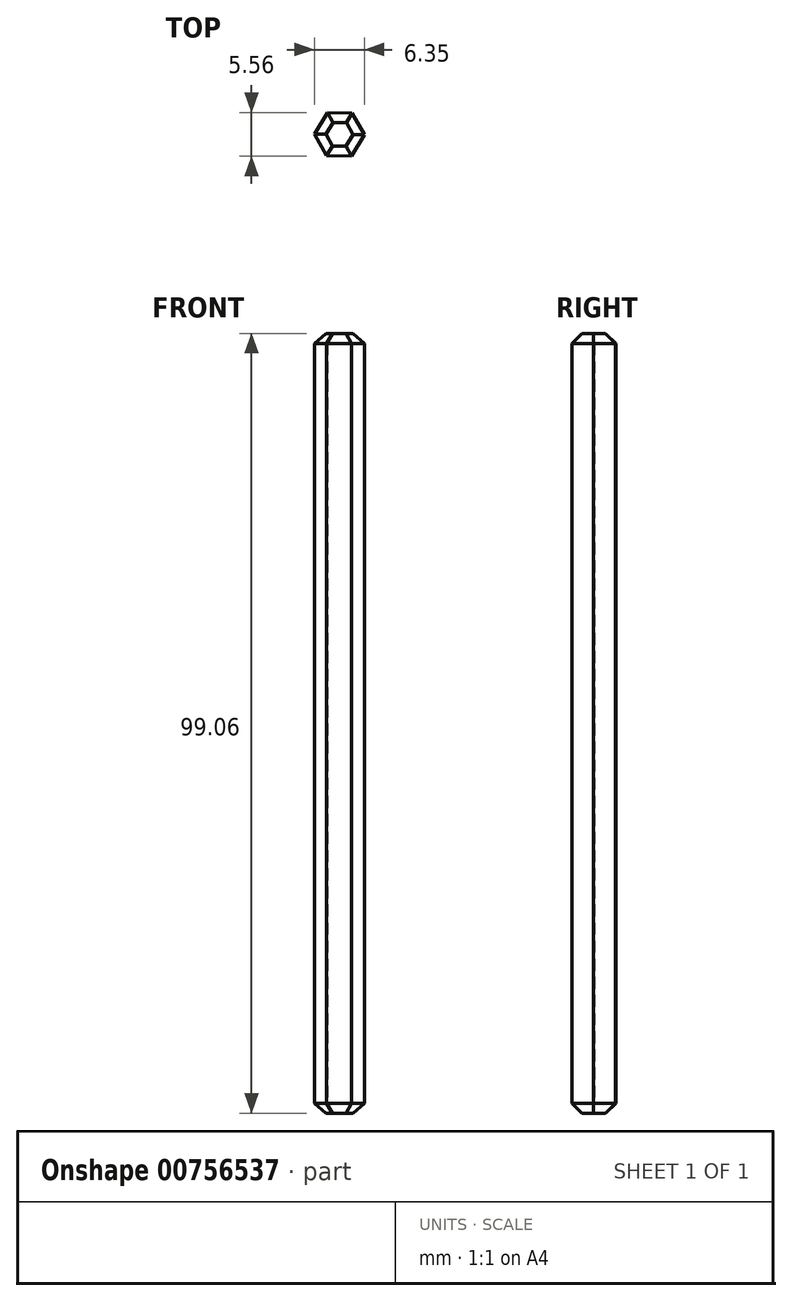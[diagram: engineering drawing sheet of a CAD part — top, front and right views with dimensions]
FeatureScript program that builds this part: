
annotation { "Feature Type Name" : "Feature", "Feature Type Description" : "" }
export const myFeature = defineFeature(function(context is Context, id is Id, definition is map)
    precondition{}
    {
        {
            var Q0;
            Q0=qCreatedBy(makeId("Top.planeOp"),FACE);
            var sketch = newSketch(context, id + "F0", { "sketchPlane" : qUnion([Q0])});
            skCircle(sketch, "E0.cCircle", {"center": v(-0.05, 1.05) * mm, "radius": 3.18 * mm, "construction": true});
            skLineSegment(sketch, "E0.0", {"start": v(-1.69, -1.67) * mm, "end": v(-3.22, 1.1) * mm});
            skLineSegment(sketch, "E0.1", {"start": v(-3.22, 1.1) * mm, "end": v(-1.58, 3.83) * mm});
            skLineSegment(sketch, "E0.2", {"start": v(-1.58, 3.83) * mm, "end": v(1.59, 3.77) * mm});
            skLineSegment(sketch, "E0.3", {"start": v(1.59, 3.77) * mm, "end": v(3.13, 0.99) * mm});
            skLineSegment(sketch, "E0.4", {"start": v(3.13, 0.99) * mm, "end": v(1.49, -1.73) * mm});
            skLineSegment(sketch, "E0.5", {"start": v(1.49, -1.73) * mm, "end": v(-1.69, -1.67) * mm});
            skSolve(sketch);
        }
        {
            var Q0;
            Q0=makeQuery(id+"F0.imprint","IMPRINT",FACE,{"disambiguationData":[TD([[makeQuery(id+"F0.imprint","IMPRINT",EDGE,{"derivedFrom":sQuery(id+"F0.wireOp",EDGE,"E0.0")}),-1.0]])]});
            extrude(context, id + "F1", {"entities" : qUnion([Q0]), "depth" : 99.06 * mm, "offsetDistance" : 25.4 * mm});
        }
        {
            var Q0;
            Q0=makeQuery(id+"F1.opExtrude","CAP_FACE",FACE,{"disambiguationData":[OSD([sQuery(id+"F0.wireOp",EDGE,"E0.0"),sQuery(id+"F0.wireOp",EDGE,"E0.1"),sQuery(id+"F0.wireOp",EDGE,"E0.2"),sQuery(id+"F0.wireOp",EDGE,"E0.3"),sQuery(id+"F0.wireOp",EDGE,"E0.4"),sQuery(id+"F0.wireOp",EDGE,"E0.5")])],"isStart":true});
            var Q1;
            Q1=makeQuery(id+"F1.opExtrude","CAP_FACE",FACE,{"disambiguationData":[OSD([sQuery(id+"F0.wireOp",EDGE,"E0.0"),sQuery(id+"F0.wireOp",EDGE,"E0.1"),sQuery(id+"F0.wireOp",EDGE,"E0.2"),sQuery(id+"F0.wireOp",EDGE,"E0.3"),sQuery(id+"F0.wireOp",EDGE,"E0.4"),sQuery(id+"F0.wireOp",EDGE,"E0.5")])],"isStart":false});
            chamfer(context, id + "F2", {"entities" : qUnion([Q0, Q1]), "width" : 1.27 * mm, "tangentPropagation" : true});
        }
    });
